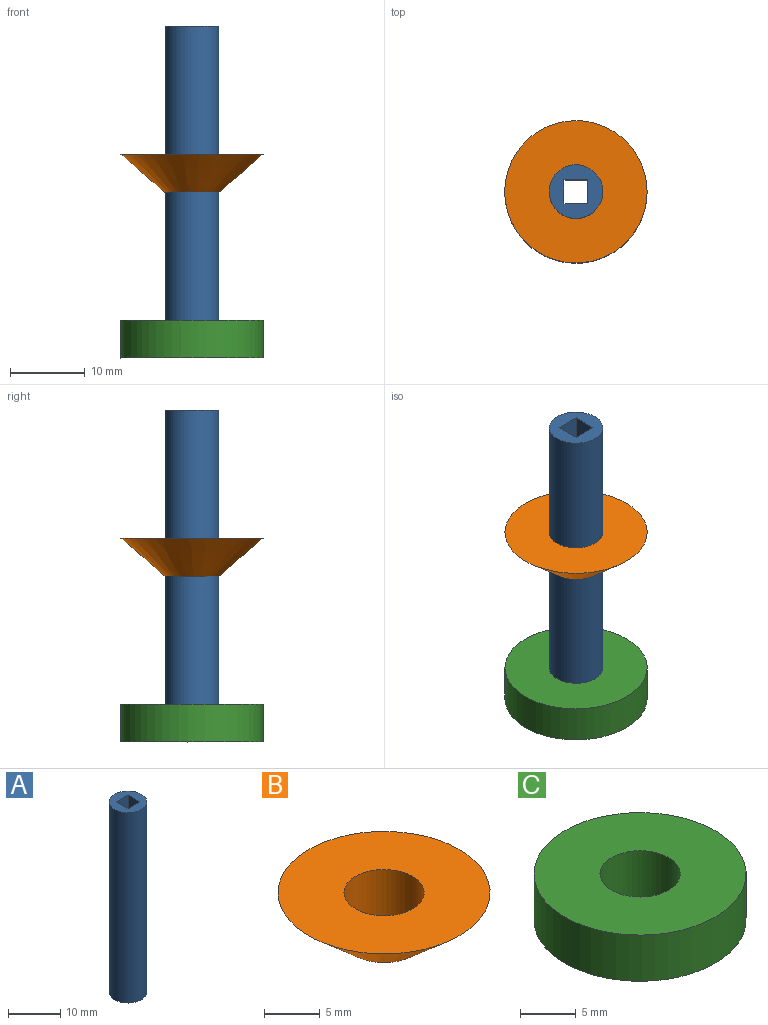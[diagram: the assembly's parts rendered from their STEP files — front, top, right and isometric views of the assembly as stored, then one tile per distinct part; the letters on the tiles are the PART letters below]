
ASSEMBLY  parts=3 mates=2
PART A: 7 faces, bbox 7.2x7.2x44.5 mm
  f0: cylinder r=3.6mm len=44.45mm, axis (0,0,-1), area 1005.4mm2, adj f1,f2
  f1: plane 7.2x7.2mm, normal (0,0,1), area 30.5mm2, adj f0,f3,f4,f5,f6
  f2: plane 7.2x7.2mm, normal (0,0,-1), area 30.5mm2, adj f0,f3,f4,f5,f6
  f3: plane 44.45x3.2mm, normal (-1,0,0), area 142.2mm2, adj f1,f2,f4,f6
  f4: plane 44.45x3.2mm, normal (0,1,0), area 142.2mm2, adj f1,f2,f3,f5
  f5: plane 44.45x3.2mm, normal (1,0,0), area 142.2mm2, adj f1,f2,f4,f6
  f6: plane 44.45x3.2mm, normal (0,-1,0), area 142.2mm2, adj f1,f2,f3,f5
PART B: 4 faces, bbox 19.1x19.1x5.1 mm
  f0: cylinder r=3.6mm len=7.2mm, axis (0,0,-1), area 114.9mm2, adj f1,f2
  f1: plane 19.05x19.05mm, normal (0,0,1), area 244.3mm2, adj f0,f3
  f2: plane 7.37x7.37mm, normal (0,0,-1), area 1.9mm2, adj f0,f3
  f3: cone r=9.53mm half-angle=49deg, axis (0,0,1), area 321.2mm2, adj f1,f2
PART C: 4 faces, bbox 19.1x19.1x5.1 mm
  f0: cylinder r=9.53mm len=19.05mm, axis (0,0,-1), area 304mm2, adj f1,f2
  f1: plane 19.05x19.05mm, normal (0,0,1), area 244.3mm2, adj f0,f3
  f2: plane 19.05x19.05mm, normal (0,0,-1), area 244.3mm2, adj f0,f3
  f3: cylinder r=3.6mm len=7.2mm, axis (0,0,-1), area 114.9mm2, adj f1,f2
PLACE A t=(11.62,6.17,-14.78)mm
PLACE B t=(11.62,6.17,-37.01)mm
PLACE C t=(49.37,-0.11,-14.78)mm
MATE fastened C.f0 <-> A.f0  axis (0,0,-1) through (11.62,6.17,-14.78)mm
MATE fastened B.f0 <-> A.f0  axis (0,0,-1) through (11.62,6.17,7.44)mm
